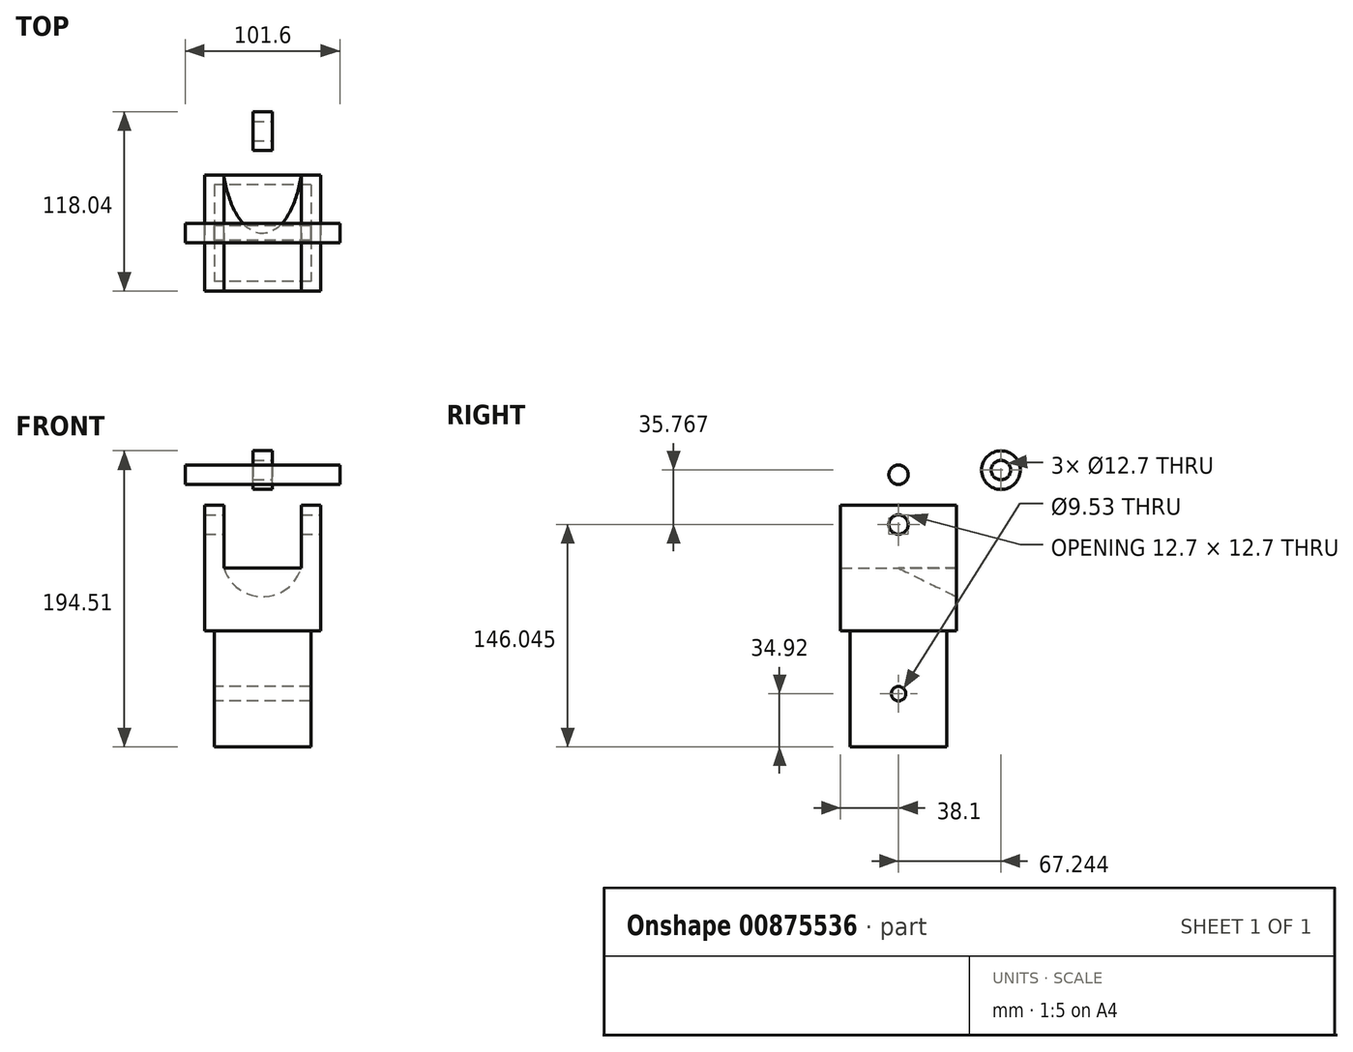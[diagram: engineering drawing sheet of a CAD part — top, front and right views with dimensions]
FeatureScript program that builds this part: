
annotation { "Feature Type Name" : "Feature", "Feature Type Description" : "" }
export const myFeature = defineFeature(function(context is Context, id is Id, definition is map)
    precondition{}
    {
        {
            var Q0;
            Q0=qCreatedBy(makeId("Top.planeOp"),FACE);
            var sketch = newSketch(context, id + "F0", { "sketchPlane" : qUnion([Q0])});
            skLineSegment(sketch, "E0.bottom", {"start": v(38.1, -38.1) * mm, "end": v(-38.1, -38.1) * mm});
            skLineSegment(sketch, "E0.top", {"start": v(38.1, 38.1) * mm, "end": v(-38.1, 38.1) * mm});
            skLineSegment(sketch, "E0.left", {"start": v(38.1, -38.1) * mm, "end": v(38.1, 38.1) * mm});
            skLineSegment(sketch, "E0.right", {"start": v(-38.1, -38.1) * mm, "end": v(-38.1, 38.1) * mm});
            skPoint(sketch, "E0.middle", {"position": v(0, 0) * mm});
            skSolve(sketch);
        }
        {
            var Q0;
            Q0=makeQuery(id+"F0.imprint","IMPRINT",FACE,{"disambiguationData":[TD([[makeQuery(id+"F0.imprint","IMPRINT",EDGE,{"derivedFrom":sQuery(id+"F0.wireOp",EDGE,"E0.bottom")}),-1.0]])]});
            extrude(context, id + "F1", {"entities" : qUnion([Q0]), "endBound" : BoundingType.SYMMETRIC, "depth" : 82.55 * mm, "offsetDistance" : 25.4 * mm});
        }
        {
            var Q0;
            Q0=qCreatedBy(makeId("Front.planeOp"),FACE);
            var sketch = newSketch(context, id + "F2", { "sketchPlane" : qUnion([Q0])});
            skLineSegment(sketch, "E1.bottom", {"start": v(25.4, 0) * mm, "end": v(-25.4, 0) * mm});
            skLineSegment(sketch, "E1.top", {"start": v(25.4, 41.28) * mm, "end": v(-25.4, 41.28) * mm});
            skLineSegment(sketch, "E1.left", {"start": v(25.4, 0) * mm, "end": v(25.4, 41.28) * mm});
            skLineSegment(sketch, "E1.right", {"start": v(-25.4, 0) * mm, "end": v(-25.4, 41.28) * mm});
            skPoint(sketch, "E1.middle", {"position": v(0, 20.64) * mm});
            skSolve(sketch);
        }
        {
            var Q0;
            Q0 = qSketchRegion(id + "F2", true);
            extrude(context, id + "F3", {"entities" : qUnion([Q0]), "operationType" : NewBodyOperationType.REMOVE, "endBound" : BoundingType.SYMMETRIC, "depth" : 76.2 * mm, "offsetDistance" : 25.4 * mm});
        }
        {
            var Q0;
            Q0=qCreatedBy(makeId("Right.planeOp"),FACE);
            var sketch = newSketch(context, id + "F4", { "sketchPlane" : qUnion([Q0])});
            skCircle(sketch, "E2", {"center": v(0, 28.58) * mm, "radius": 6.35 * mm});
            skSolve(sketch);
        }
        {
            var Q0;
            Q0 = qSketchRegion(id + "F4", true);
            extrude(context, id + "F5", {"entities" : qUnion([Q0]), "operationType" : NewBodyOperationType.REMOVE, "endBound" : BoundingType.SYMMETRIC, "oppositeDirection" : true, "depth" : 76.2 * mm, "offsetDistance" : 25.4 * mm});
        }
        {
            var Q0;
            Q0=qCreatedBy(makeId("Right.planeOp"),FACE);
            var sketch = newSketch(context, id + "F6", { "sketchPlane" : qUnion([Q0])});
            skLineSegment(sketch, "E3", {"start": v(38.1, -18.8) * mm, "end": v(-37.7, 18.43) * mm});
            skSolve(sketch);
        }
        {
            var Q0;
            Q0=makeQuery(id+"F1.opExtrude","SWEPT_FACE",FACE,{"disambiguationData":[OSD([sQuery(id+"F0.wireOp",EDGE,"E0.top")])]});
            var sketch = newSketch(context, id + "F7", { "sketchPlane" : qUnion([Q0])});
            skArc(sketch, "E4", {"start": v(-25.4, 0) * mm, "mid": v(0, -18.8) * mm, "end": v(25.4, 0) * mm});
            skSolve(sketch);
        }
        {
            var Q0;
            Q0=makeQuery(id+"F7.imprint","IMPRINT",FACE,{"disambiguationData":[TD([[makeQuery(id+"F7.imprint","IMPRINT",EDGE,{"derivedFrom":sQuery(id+"F7.wireOp",EDGE,"E4")}),1.0]])]});
            var Q1;
            Q1=sQuery(id+"F6.wireOp",EDGE,"E3");
            sweep(context, id + "F8", {"operationType" : NewBodyOperationType.REMOVE, "profiles" : qUnion([Q0]), "path" : qUnion([Q1])});
        }
        {
            var Q0;
            Q0=makeQuery(id+"F1.opExtrude","CAP_FACE",FACE,{"disambiguationData":[OSD([sQuery(id+"F0.wireOp",EDGE,"E0.bottom"),sQuery(id+"F0.wireOp",EDGE,"E0.top"),sQuery(id+"F0.wireOp",EDGE,"E0.left"),sQuery(id+"F0.wireOp",EDGE,"E0.right")])],"isStart":true});
            var sketch = newSketch(context, id + "F9", { "sketchPlane" : qUnion([Q0])});
            skLineSegment(sketch, "E5.bottom", {"start": v(31.75, -31.75) * mm, "end": v(-31.75, -31.75) * mm});
            skLineSegment(sketch, "E5.top", {"start": v(31.75, 31.75) * mm, "end": v(-31.75, 31.75) * mm});
            skLineSegment(sketch, "E5.left", {"start": v(31.75, -31.75) * mm, "end": v(31.75, 31.75) * mm});
            skLineSegment(sketch, "E5.right", {"start": v(-31.75, -31.75) * mm, "end": v(-31.75, 31.75) * mm});
            skPoint(sketch, "E5.middle", {"position": v(0, 0) * mm});
            skSolve(sketch);
        }
        {
            var Q0;
            Q0=makeQuery(id+"F9.imprint","IMPRINT",FACE,{"disambiguationData":[TD([[makeQuery(id+"F9.imprint","IMPRINT",EDGE,{"derivedFrom":sQuery(id+"F9.wireOp",EDGE,"E5.bottom")}),-1.0]])]});
            extrude(context, id + "F10", {"entities" : qUnion([Q0]), "operationType" : NewBodyOperationType.ADD, "depth" : 76.2 * mm, "offsetDistance" : 25.4 * mm});
        }
        {
            var Q0;
            Q0=makeQuery(id+"F10.opExtrude","SWEPT_FACE",FACE,{"disambiguationData":[OSD([sQuery(id+"F9.wireOp",EDGE,"E5.right")])]});
            var sketch = newSketch(context, id + "F11", { "sketchPlane" : qUnion([Q0])});
            skLineSegment(sketch, "E6", {"start": v(0, -41.28) * mm, "end": v(0, -82.55) * mm});
            skCircle(sketch, "E7", {"center": v(0, -82.55) * mm, "radius": 4.76 * mm});
            skSolve(sketch);
        }
        {
            var Q0;
            Q0=makeQuery(id+"F11.imprint","IMPRINT",FACE,{"disambiguationData":[TD([[makeQuery(id+"F11.imprint","IMPRINT",EDGE,{"derivedFrom":sQuery(id+"F11.wireOp",EDGE,"E7")}),1.0]])]});
            extrude(context, id + "F12", {"entities" : qUnion([Q0]), "operationType" : NewBodyOperationType.REMOVE, "endBound" : BoundingType.THROUGH_ALL, "oppositeDirection" : true, "depth" : 25.4 * mm, "offsetDistance" : 25.4 * mm});
        }
        {
            var Q0;
            Q0=qCreatedBy(makeId("Right.planeOp"),FACE);
            var sketch = newSketch(context, id + "F13", { "sketchPlane" : qUnion([Q0])});
            skCircle(sketch, "E8", {"center": v(0, 61.3) * mm, "radius": 6.35 * mm});
            skSolve(sketch);
        }
        {
            var Q0;
            Q0=makeQuery(id+"F13.imprint","IMPRINT",FACE,{"disambiguationData":[TD([[makeQuery(id+"F13.imprint","IMPRINT",EDGE,{"derivedFrom":sQuery(id+"F13.wireOp",EDGE,"E8")}),1.0]])]});
            extrude(context, id + "F14", {"entities" : qUnion([Q0]), "endBound" : BoundingType.SYMMETRIC, "depth" : 101.6 * mm, "offsetDistance" : 25.4 * mm});
        }
        {
            var Q0;
            Q0=qCreatedBy(makeId("Right.planeOp"),FACE);
            var sketch = newSketch(context, id + "F15", { "sketchPlane" : qUnion([Q0])});
            skCircle(sketch, "E9", {"center": v(67.24, 64.34) * mm, "radius": 6.35 * mm});
            skCircle(sketch, "E10", {"center": v(67.24, 64.34) * mm, "radius": 12.7 * mm});
            skSolve(sketch);
        }
        {
            var Q0;
            Q0=makeQuery(id+"F15.imprint","IMPRINT",FACE,{"disambiguationData":[TD([[makeQuery(id+"F15.imprint","IMPRINT",EDGE,{"derivedFrom":sQuery(id+"F15.wireOp",EDGE,"E9")}),-1.0]])]});
            extrude(context, id + "F16", {"entities" : qUnion([Q0]), "operationType" : NewBodyOperationType.ADD, "endBound" : BoundingType.SYMMETRIC, "oppositeDirection" : true, "depth" : 12.7 * mm, "offsetDistance" : 25.4 * mm});
        }
    });
